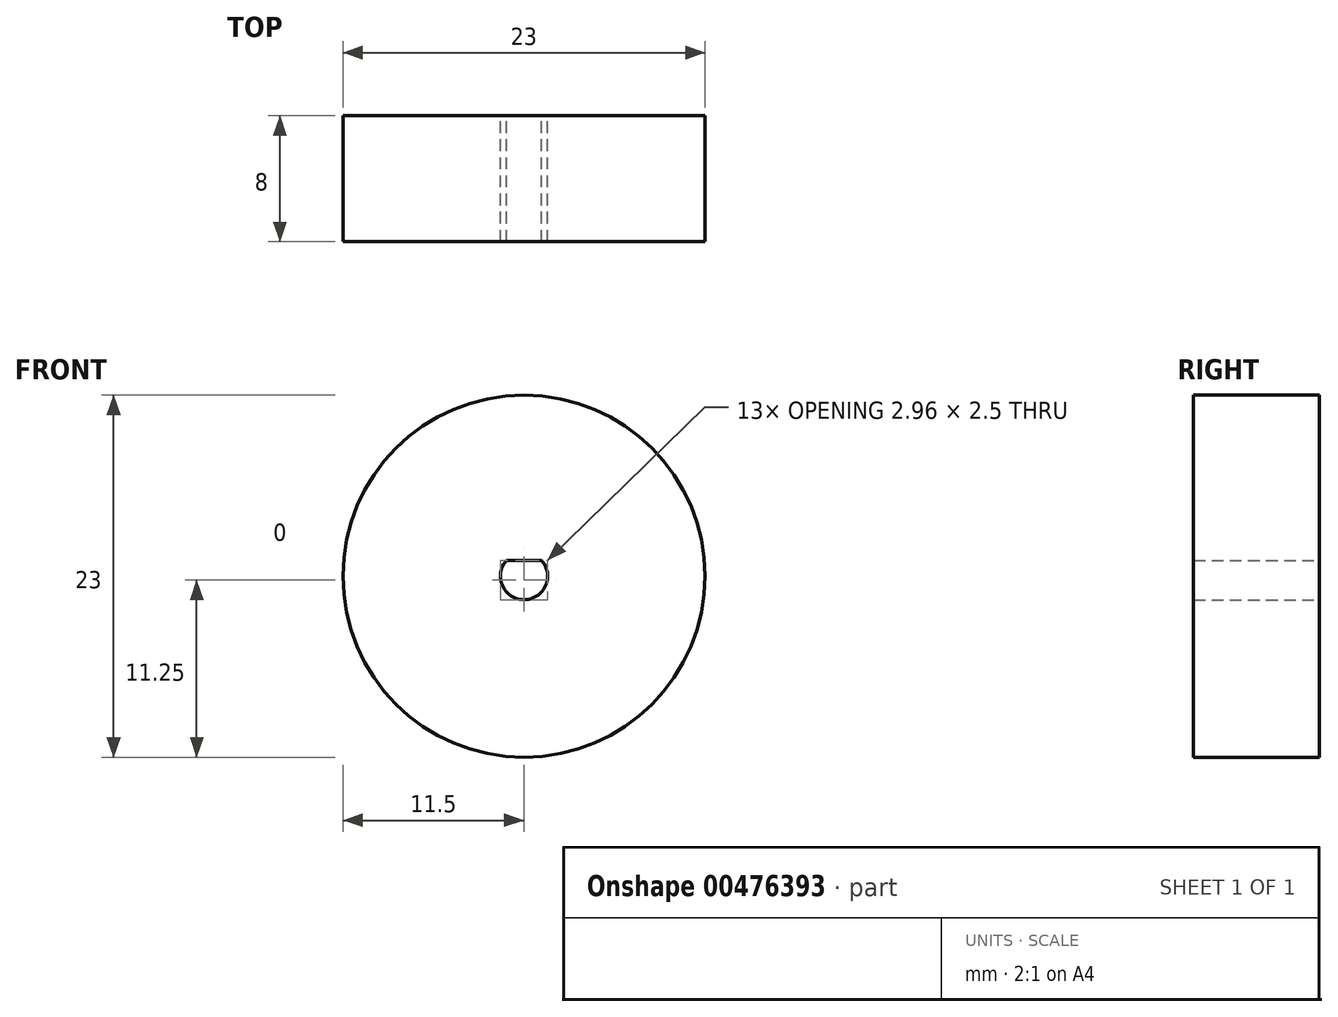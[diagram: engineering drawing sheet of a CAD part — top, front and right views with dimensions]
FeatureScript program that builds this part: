
annotation { "Feature Type Name" : "Feature", "Feature Type Description" : "" }
export const myFeature = defineFeature(function(context is Context, id is Id, definition is map)
    precondition{}
    {
        {
            var Q0;
            Q0=qCreatedBy(makeId("Front.planeOp"),FACE);
            var sketch = newSketch(context, id + "F0", { "sketchPlane" : qUnion([Q0])});
            skCircle(sketch, "E0", {"center": v(0, 0) * mm, "radius": 11.5 * mm});
            skArc(sketch, "E1", {"start": v(-1.12, 1) * mm, "mid": v(0, -1.5) * mm, "end": v(1.12, 1) * mm});
            skLineSegment(sketch, "E2", {"start": v(-1.12, 1) * mm, "end": v(1.12, 1) * mm});
            skSolve(sketch);
        }
        {
            var Q0;
            Q0=qSketchRegion(id+"F0",true);
            extrude(context, id + "F1", {"entities" : qUnion([Q0]), "depth" : 8 * mm});
        }
    });
